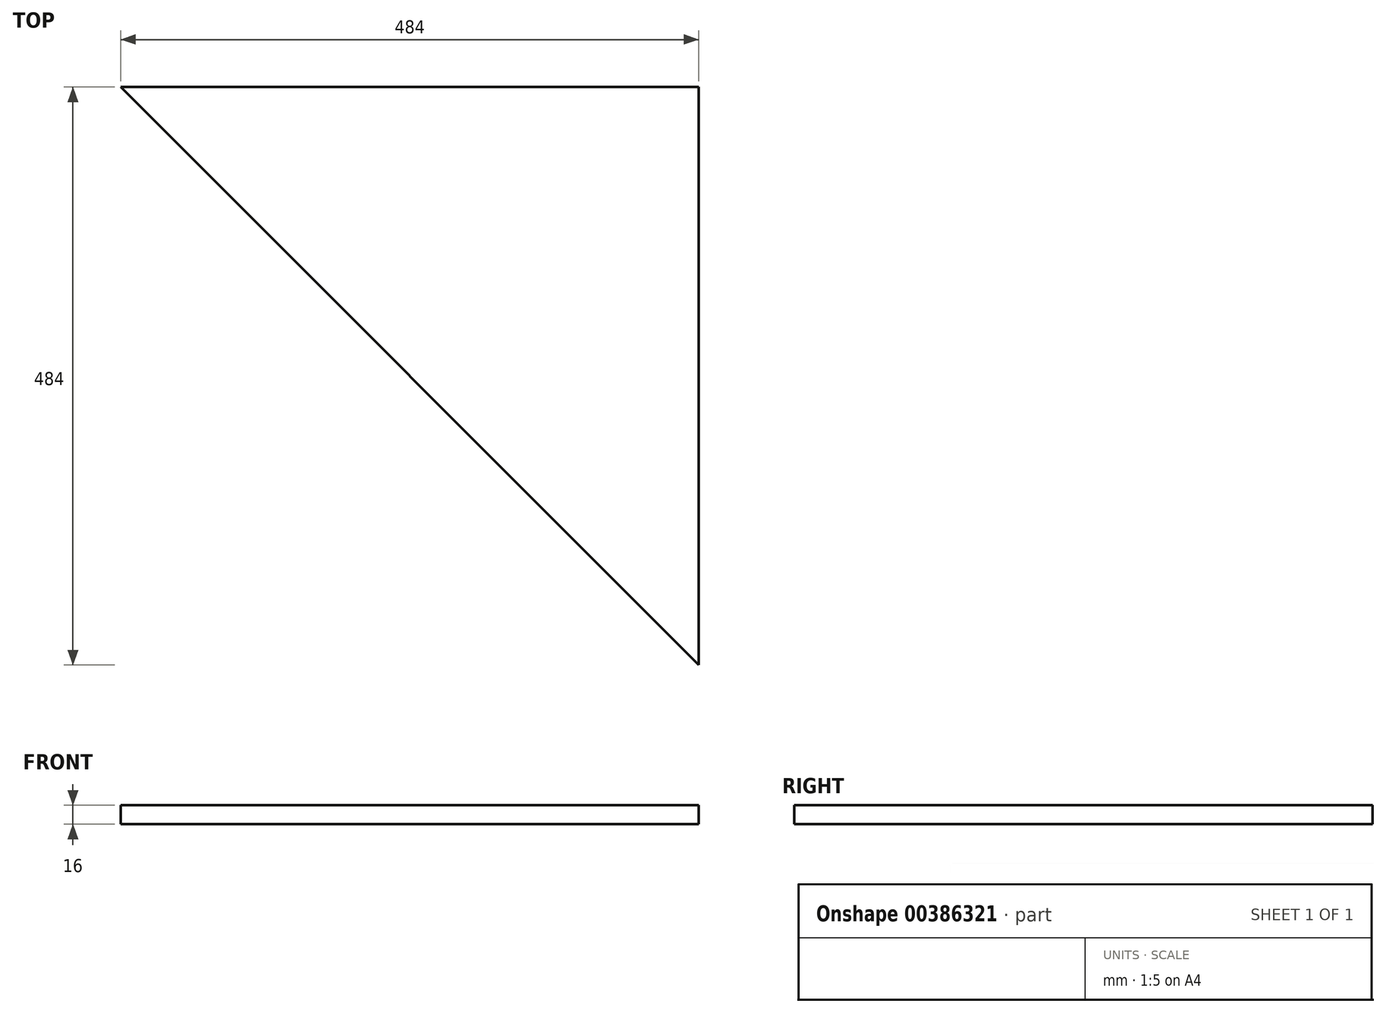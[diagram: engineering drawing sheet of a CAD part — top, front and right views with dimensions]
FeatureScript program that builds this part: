
annotation { "Feature Type Name" : "Feature", "Feature Type Description" : "" }
export const myFeature = defineFeature(function(context is Context, id is Id, definition is map)
    precondition{}
    {
        {
            var Q0;
            Q0=qCreatedBy(makeId("Top.planeOp"),FACE);
            var sketch = newSketch(context, id + "F0", { "sketchPlane" : qUnion([Q0])});
            skCircle(sketch, "E0", {"center": v(-41.67, 0) * mm, "radius": 500 * mm});
            skCircle(sketch, "E1", {"center": v(-41.67, 0) * mm, "radius": 484 * mm});
            skCircle(sketch, "E2.cCircle", {"center": v(-41.67, 0) * mm, "radius": 484 * mm, "construction": true});
            skLineSegment(sketch, "E2.0", {"start": v(-41.67, 484) * mm, "end": v(442.33, 0) * mm});
            skLineSegment(sketch, "E2.1", {"start": v(442.33, 0) * mm, "end": v(-41.67, -484) * mm});
            skLineSegment(sketch, "E2.2", {"start": v(-41.67, -484) * mm, "end": v(-525.67, 0) * mm});
            skLineSegment(sketch, "E2.3", {"start": v(-525.67, 0) * mm, "end": v(-41.67, 484) * mm});
            skLineSegment(sketch, "E3", {"start": v(-41.67, 484) * mm, "end": v(-41.67, -484) * mm});
            skLineSegment(sketch, "E4", {"start": v(-525.67, 0) * mm, "end": v(442.33, 0) * mm});
            skLineSegment(sketch, "E5", {"start": v(-525.67, 0) * mm, "end": v(-541.67, 0) * mm});
            skLineSegment(sketch, "E6", {"start": v(-41.67, 484) * mm, "end": v(-41.67, 500) * mm});
            skLineSegment(sketch, "E7", {"start": v(-41.67, -484) * mm, "end": v(-41.67, -500) * mm});
            skLineSegment(sketch, "E8", {"start": v(442.33, 0) * mm, "end": v(458.33, 0) * mm});
            skLineSegment(sketch, "E9.2", {"start": v(442.33, 0) * mm, "end": v(-41.67, 484) * mm});
            skLineSegment(sketch, "E10.bottom", {"start": v(-525.67, 0) * mm, "end": v(-41.67, 0) * mm});
            skLineSegment(sketch, "E10.right", {"start": v(-41.67, 0) * mm, "end": v(-41.67, 484) * mm});
            skLineSegment(sketch, "E11.right", {"start": v(-41.67, 0) * mm, "end": v(-41.67, -484) * mm});
            skLineSegment(sketch, "E12.bottom", {"start": v(-41.67, 0) * mm, "end": v(458.33, 0) * mm});
            skLineSegment(sketch, "E12.top", {"start": v(-41.67, 0) * mm, "end": v(458.33, 0) * mm});
            skLineSegment(sketch, "E12.left", {"start": v(-41.67, 0) * mm, "end": v(-41.67, 0) * mm});
            skLineSegment(sketch, "E12.right", {"start": v(458.33, 0) * mm, "end": v(458.33, 0) * mm});
            skLineSegment(sketch, "E13.top", {"start": v(-41.67, 0) * mm, "end": v(442.33, 0) * mm});
            skLineSegment(sketch, "E13.left", {"start": v(-41.67, -484) * mm, "end": v(-41.67, 0) * mm});
            skSolve(sketch);
        }
        {
            var Q0;
            Q0=makeQuery(id+"F0.imprint","IMPRINT",FACE,{"disambiguationData":[TD([[makeQuery(id+"F0.imprint","IMPRINT",EDGE,{"derivedFrom":sQuery(id+"F0.wireOp",EDGE,"E2.2")}),-1.0]])]});
            extrude(context, id + "F1", {"entities" : qUnion([Q0]), "depth" : 16 * mm});
        }
    });
